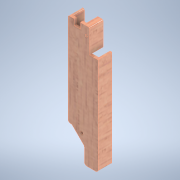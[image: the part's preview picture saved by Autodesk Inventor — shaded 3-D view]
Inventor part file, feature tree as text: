
AUTODESK INVENTOR PART (.ipt)
format: ipt  version: 2021 (Build 250183000, 183)  size: 279,040 bytes
history: native  units: mm
features: sketch x14, extrude x10, reference x5, hole x3, projected_geometry x3, other x3, plane x1
ambient origin geometry x8: Origin, YZ Plane, XZ Plane, XY Plane, X Axis, Y Axis, Z Axis, Center Point
bodies: Volumenkörper1 (feature_tree)
feature tree (39):
  sketch  "Skizze1"  dims[d0=9.0mm d1=0.0mm d2=2.0mm d3=0.0mm]
  plane  "Arbeitsebene1"
  extrude  "Extrusion1"  Depth=2.0mm TaperAngle=0.0deg
  extrude  "Extrusion2"  Depth=5.0mm
  extrude  "Extrusion3"  Depth=1.0mm TaperAngle=0.0deg
  extrude  "Extrusion4"  Depth=3.8mm
  extrude  "Extrusion5"  Depth=3.0mm
  extrude  "Extrusion6"  Depth=9.0mm
  extrude  "Extrusion7"  Depth=1.5mm
  extrude  "Extrusion8"  TaperAngle=0.0deg  [1 undecoded]
  extrude  "Extrusion9"  Depth=5.0mm
  hole  "Bohrung1"  [1 undecoded]
  hole  "Bohrung2"  [1 undecoded]
  hole  "Bohrung3"  [1 undecoded]
  extrude  "Extrusion11"  Depth=2.5mm
  sketch  "Skizze2"  dims[d4=5.0mm d5=5.0mm]
  reference  "Referenz1"
  reference  "Referenz2"
  reference  "Referenz3"
  reference  "Referenz4"
  sketch  "Skizze3"  dims[d6=2.5mm d7=0.0mm d8=1.0mm d9=0.0mm]
  projected_geometry  "Projizierte Kontur1"
  projected_geometry  "Projizierte Kontur2"
  reference  "Referenz5"
  sketch  "Skizze5"  dims[d10=2.0mm d11=3.8mm]
  projected_geometry  "Projizierte Kontur3"
  sketch  "Skizze6"  dims[d12=1.0mm d13=0.0mm d14=3.0mm]
  sketch  "Skizze7"  dims[d15=0.0mm d16=0.0mm d17=9.0mm]
  sketch  "Skizze8"  dims[d18=3.0mm d19=0.0mm d20=1.5mm]
  sketch  "Skizze9"  dims[d21=14.7mm d23=0.0mm d24=0.0mm]
  sketch  "Skizze10"  dims[d25=4.9mm d26=5.0mm]
  sketch  "Skizze11"  dims[d27=4.8mm d28=3.0mm d29=0.0mm]
  sketch  "Skizze12"  dims[d30=4.0mm d31=4.0mm]
  sketch  "Skizze13"  dims[d32=2.0mm d33=6.0mm d34=4.0mm d35=2.0mm d36=90.0deg d37=8.0mm d38=20.594885mm d39=2.5mm]
  sketch  "Skizze14"  dims[d40=7.0mm]
  sketch  "Skizze16"  dims[d41=2.0mm d42=6.0mm d43=4.0mm d44=2.0mm d45=90.0deg d46=8.0mm d47=20.594885mm d48=2.5mm d49=2.5mm d50=2.5mm d51=6.0mm d52=4.0mm d53=2.0mm d54=90.0deg d55=8.0mm d56=20.594885mm d57=23.8mm d63=0.5mm d64=10.0mm d65=10.0mm d66=0.0mm]
  other  "Baugruppe1.iam"
  other  "Case_DIP:1"
  other  "Baugruppe1"
note: 4 required parameter values undecoded (feature->parameter linkage not recoverable at this tier; creation-order binding heuristic only, values carry confidence <= 0.55)
